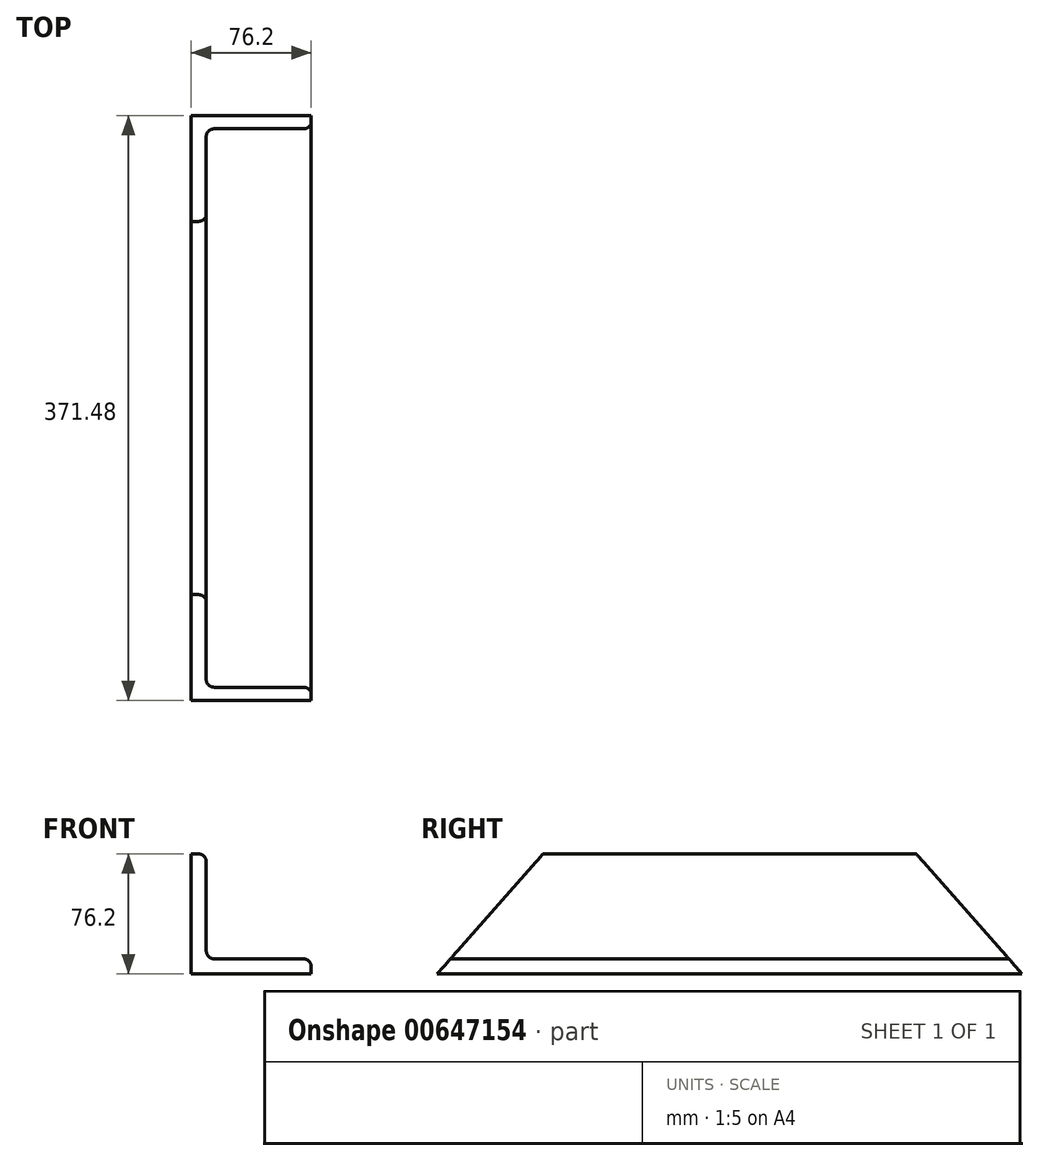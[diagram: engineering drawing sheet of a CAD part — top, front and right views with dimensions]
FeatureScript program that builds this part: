
annotation { "Feature Type Name" : "Feature", "Feature Type Description" : "" }
export const myFeature = defineFeature(function(context is Context, id is Id, definition is map)
    precondition{}
    {
        {
            var Q0;
            Q0=qCreatedBy(makeId("Front.planeOp"),FACE);
            var sketch = newSketch(context, id + "F0", { "sketchPlane" : qUnion([Q0])});
            skLineSegment(sketch, "E0.bottom", {"start": v(0, 0) * mm, "end": v(76.2, 0) * mm});
            skLineSegment(sketch, "E0.top", {"start": v(0, 76.2) * mm, "end": v(9.52, 76.2) * mm});
            skLineSegment(sketch, "E0.left", {"start": v(0, 0) * mm, "end": v(0, 76.2) * mm});
            skLineSegment(sketch, "E0.right", {"start": v(76.2, 0) * mm, "end": v(76.2, 9.53) * mm});
            skLineSegment(sketch, "E1.0", {"start": v(9.52, 9.52) * mm, "end": v(9.52, 76.2) * mm});
            skLineSegment(sketch, "E2.0", {"start": v(9.52, 9.53) * mm, "end": v(76.2, 9.53) * mm});
            skSolve(sketch);
        }
        {
            var Q0;
            Q0 = qSketchRegion(id + "F0", true);
            extrude(context, id + "F1", {"entities" : qUnion([Q0]), "endBound" : BoundingType.SYMMETRIC, "depth" : 371.47 * mm, "offsetDistance" : 25.4 * mm});
        }
        {
            var Q0;
            Q0=makeQuery(id+"F1.opExtrude","SWEPT_FACE",FACE,{"disambiguationData":[OSD([sQuery(id+"F0.wireOp",EDGE,"E0.left")])]});
            var sketch = newSketch(context, id + "F2", { "sketchPlane" : qUnion([Q0])});
            skPoint(sketch, "E3.0", {"position": v(185.74, 0) * mm});
            skPoint(sketch, "E4.0", {"position": v(-185.74, 0) * mm});
            skLineSegment(sketch, "E5", {"start": v(-185.74, 0) * mm, "end": v(-118.56, 76.2) * mm});
            skLineSegment(sketch, "E6", {"start": v(-118.56, 76.2) * mm, "end": v(-185.74, 76.2) * mm});
            skLineSegment(sketch, "E7", {"start": v(-185.74, 76.2) * mm, "end": v(-185.74, 0) * mm});
            skLineSegment(sketch, "E8.MirrorCS", {"start": v(185.74, 0) * mm, "end": v(118.56, 76.2) * mm});
            skLineSegment(sketch, "E9.MirrorCS", {"start": v(118.56, 76.2) * mm, "end": v(185.74, 76.2) * mm});
            skLineSegment(sketch, "E10.MirrorCS", {"start": v(185.74, 76.2) * mm, "end": v(185.74, 0) * mm});
            skSolve(sketch);
        }
        {
            var Q0;
            Q0 = qSketchRegion(id + "F2", true);
            extrude(context, id + "F3", {"entities" : qUnion([Q0]), "operationType" : NewBodyOperationType.REMOVE, "oppositeDirection" : true, "depth" : 76.2 * mm, "offsetDistance" : 25.4 * mm});
        }
        {
            var Q0;
            Q0=makeQuery(id+"F1.opExtrude","SWEPT_EDGE",EDGE,{"disambiguationData":[OSD([sQuery(id+"F0.wireOp",EDGE,"E0.top"),sQuery(id+"F0.wireOp",EDGE,"E1.0")])]});
            var Q1;
            Q1=makeQuery(id+"F1.opExtrude","SWEPT_EDGE",EDGE,{"disambiguationData":[OSD([sQuery(id+"F0.wireOp",EDGE,"E1.0"),sQuery(id+"F0.wireOp",EDGE,"E2.0")])]});
            var Q2;
            Q2=makeQuery(id+"F1.opExtrude","SWEPT_EDGE",EDGE,{"disambiguationData":[OSD([sQuery(id+"F0.wireOp",EDGE,"E0.right"),sQuery(id+"F0.wireOp",EDGE,"E2.0")])]});
            fillet(context, id + "F4", {"entities" : qUnion([Q0, Q1, Q2]), "radius" : 5.08 * mm, "tangentPropagation" : true, "allowEdgeOverflow" : false});
        }
    });
